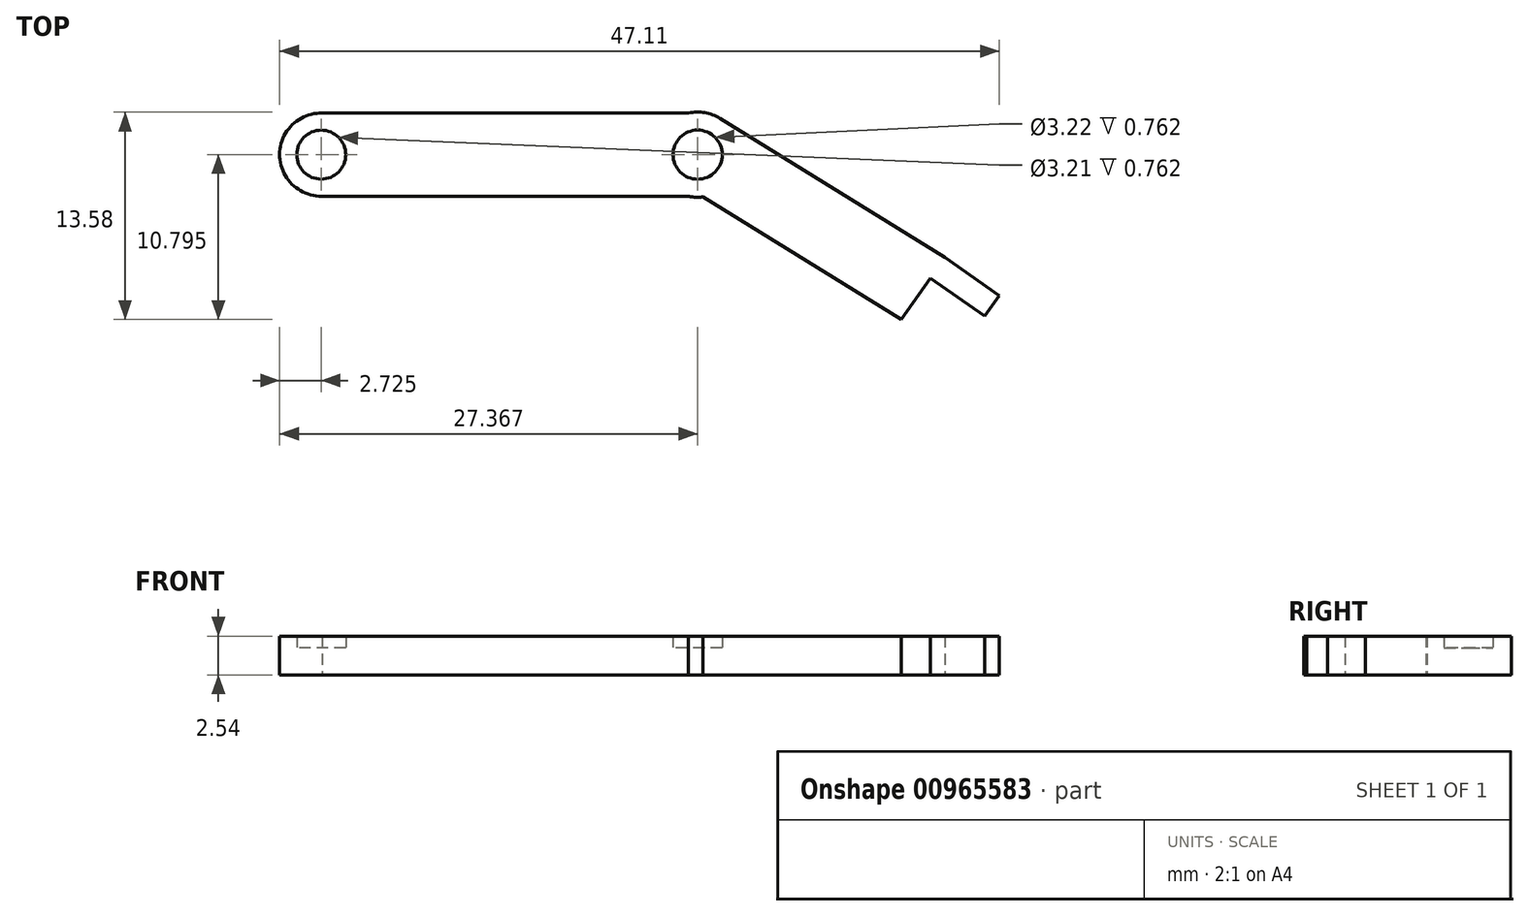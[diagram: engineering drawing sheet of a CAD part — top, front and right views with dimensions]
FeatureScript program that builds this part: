
annotation { "Feature Type Name" : "Feature", "Feature Type Description" : "" }
export const myFeature = defineFeature(function(context is Context, id is Id, definition is map)
    precondition{}
    {
        {
            var Q0;
            Q0=qCreatedBy(makeId("Top.planeOp"),FACE);
            var sketch = newSketch(context, id + "F0", { "sketchPlane" : qUnion([Q0])});
            skCircle(sketch, "E0", {"center": v(-60.34, 40.06) * mm, "radius": 2.73 * mm});
            skLineSegment(sketch, "E1", {"start": v(-60.4, 42.78) * mm, "end": v(-35.97, 42.78) * mm});
            skLineSegment(sketch, "E2", {"start": v(-60.31, 37.33) * mm, "end": v(-35.42, 37.33) * mm});
            skCircle(sketch, "E3", {"center": v(-35.7, 40.05) * mm, "radius": 2.79 * mm});
            skLineSegment(sketch, "E4", {"start": v(-34.22, 42.43) * mm, "end": v(-19.51, 33.31) * mm});
            skLineSegment(sketch, "E5", {"start": v(-35.42, 37.33) * mm, "end": v(-22.37, 29.26) * mm});
            skLineSegment(sketch, "E6", {"start": v(-22.37, 29.26) * mm, "end": v(-19.51, 33.31) * mm});
            skLineSegment(sketch, "E7", {"start": v(-19.51, 33.31) * mm, "end": v(-15.95, 30.81) * mm});
            skLineSegment(sketch, "E8", {"start": v(-15.95, 30.81) * mm, "end": v(-16.9, 29.47) * mm});
            skLineSegment(sketch, "E9", {"start": v(-16.9, 29.47) * mm, "end": v(-20.45, 31.97) * mm});
            skCircle(sketch, "E10", {"center": v(-60.34, 40.06) * mm, "radius": 1.6 * mm});
            skCircle(sketch, "E11", {"center": v(-35.7, 40.05) * mm, "radius": 1.61 * mm});
            skSolve(sketch);
        }
        {
            var Q0;
            Q0 = qSketchRegion(id + "F0", true);
            extrude(context, id + "F1", {"entities" : qUnion([Q0]), "depth" : 2.54 * mm, "offsetDistance" : 25.4 * mm});
        }
        {
            var Q0;
            Q0=makeQuery(id+"F0.imprint","IMPRINT",FACE,{"disambiguationData":[TD([[makeQuery(id+"F0.imprint","IMPRINT",EDGE,{"derivedFrom":sQuery(id+"F0.wireOp",EDGE,"E10")}),1.0]])]});
            var Q1;
            Q1=makeQuery(id+"F0.imprint","IMPRINT",FACE,{"disambiguationData":[TD([[makeQuery(id+"F0.imprint","IMPRINT",EDGE,{"derivedFrom":sQuery(id+"F0.wireOp",EDGE,"E11")}),1.0]])]});
            extrude(context, id + "F2", {"entities" : qUnion([Q0, Q1]), "operationType" : NewBodyOperationType.ADD, "depth" : 1.78 * mm, "offsetDistance" : 25.4 * mm});
        }
    });
